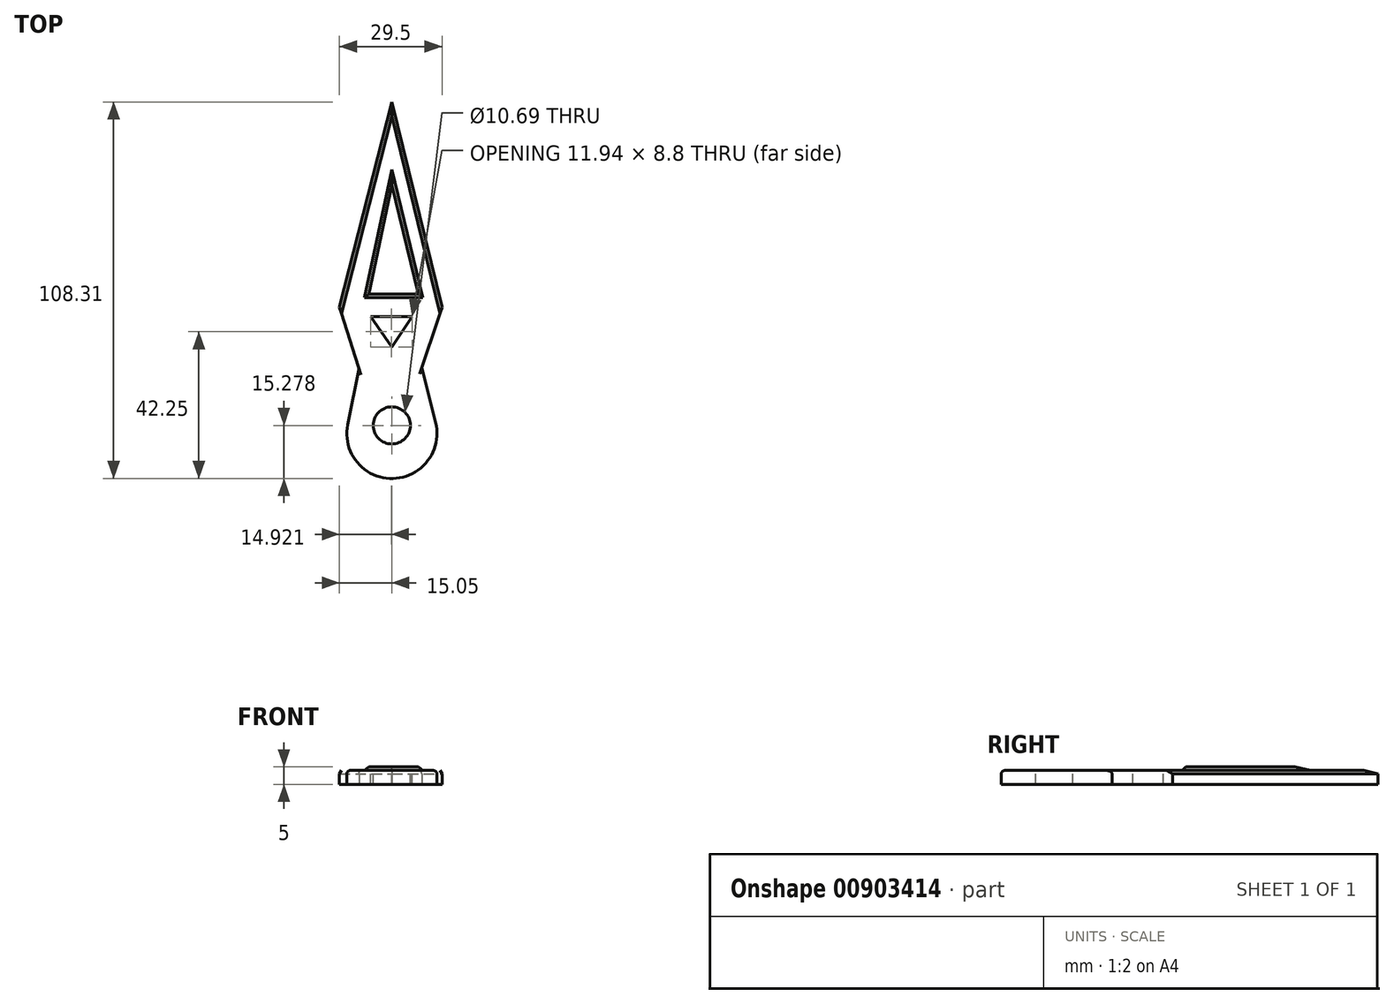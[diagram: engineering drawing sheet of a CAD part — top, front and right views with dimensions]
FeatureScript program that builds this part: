
annotation { "Feature Type Name" : "Feature", "Feature Type Description" : "" }
export const myFeature = defineFeature(function(context is Context, id is Id, definition is map)
    precondition{}
    {
        {
            var Q0;
            Q0=qCreatedBy(makeId("Top.planeOp"),FACE);
            var sketch = newSketch(context, id + "F0", { "sketchPlane" : qUnion([Q0])});
            skLineSegment(sketch, "E0", {"start": v(-15.05, 17.48) * mm, "end": v(14.45, 17.48) * mm});
            skLineSegment(sketch, "E1", {"start": v(-15.05, 17.48) * mm, "end": v(-9.45, 0) * mm});
            skCircle(sketch, "E2", {"center": v(0, -18.9) * mm, "radius": 12.95 * mm});
            skLineSegment(sketch, "E3", {"start": v(14.45, 17.48) * mm, "end": v(8.6, 0) * mm});
            skLineSegment(sketch, "E4", {"start": v(8.6, 0) * mm, "end": v(12.56, -15.73) * mm});
            skLineSegment(sketch, "E5", {"start": v(-9.45, 0) * mm, "end": v(-12.7, -16.36) * mm});
            skLineSegment(sketch, "E6", {"start": v(-15.05, 17.48) * mm, "end": v(0, 76.47) * mm});
            skLineSegment(sketch, "E7", {"start": v(0, 76.47) * mm, "end": v(14.45, 17.48) * mm});
            skSolve(sketch);
        }
        {
            var Q0;
            Q0 = qSketchRegion(id + "F0", true);
            extrude(context, id + "F1", {"entities" : qUnion([Q0]), "depth" : 4 * mm, "offsetDistance" : 25.4 * mm});
        }
        {
            var Q0;
            Q0=makeQuery(id+"F1.opExtrude","CAP_FACE",FACE,{"disambiguationData":[OSD([sQuery(id+"F0.wireOp",EDGE,"E1"),sQuery(id+"F0.wireOp",EDGE,"E2"),sQuery(id+"F0.wireOp",EDGE,"E3"),sQuery(id+"F0.wireOp",EDGE,"E4"),sQuery(id+"F0.wireOp",EDGE,"E5"),sQuery(id+"F0.wireOp",EDGE,"E6"),sQuery(id+"F0.wireOp",EDGE,"E7")])],"isStart":false});
            var sketch = newSketch(context, id + "F2", { "sketchPlane" : qUnion([Q0])});
            skCircle(sketch, "E8", {"center": v(0, -16.56) * mm, "radius": 5.34 * mm});
            skSolve(sketch);
        }
        {
            var Q0;
            Q0 = qSketchRegion(id + "F2", true);
            extrude(context, id + "F3", {"entities" : qUnion([Q0]), "operationType" : NewBodyOperationType.REMOVE, "oppositeDirection" : true, "depth" : 25.4 * mm, "offsetDistance" : 25.4 * mm});
        }
        {
            var Q0;
            Q0=makeQuery(id+"F1.opExtrude","CAP_FACE",FACE,{"disambiguationData":[OSD([sQuery(id+"F0.wireOp",EDGE,"E1"),sQuery(id+"F0.wireOp",EDGE,"E2"),sQuery(id+"F0.wireOp",EDGE,"E3"),sQuery(id+"F0.wireOp",EDGE,"E4"),sQuery(id+"F0.wireOp",EDGE,"E5"),sQuery(id+"F0.wireOp",EDGE,"E6"),sQuery(id+"F0.wireOp",EDGE,"E7")])],"isStart":false});
            var sketch = newSketch(context, id + "F4", { "sketchPlane" : qUnion([Q0])});
            skLineSegment(sketch, "E9", {"start": v(0, 6) * mm, "end": v(-6.1, 14.81) * mm});
            skLineSegment(sketch, "E10", {"start": v(-6.1, 14.81) * mm, "end": v(5.84, 14.81) * mm});
            skLineSegment(sketch, "E11", {"start": v(5.84, 14.81) * mm, "end": v(0, 6) * mm});
            skSolve(sketch);
        }
        {
            var Q0;
            Q0 = qSketchRegion(id + "F4", true);
            extrude(context, id + "F5", {"entities" : qUnion([Q0]), "operationType" : NewBodyOperationType.REMOVE, "oppositeDirection" : true, "depth" : 25.4 * mm, "offsetDistance" : 25.4 * mm});
        }
        {
            var Q0;
            Q0=makeQuery(id+"F1.opExtrude","CAP_FACE",FACE,{"disambiguationData":[OSD([sQuery(id+"F0.wireOp",EDGE,"E1"),sQuery(id+"F0.wireOp",EDGE,"E2"),sQuery(id+"F0.wireOp",EDGE,"E3"),sQuery(id+"F0.wireOp",EDGE,"E4"),sQuery(id+"F0.wireOp",EDGE,"E5"),sQuery(id+"F0.wireOp",EDGE,"E6"),sQuery(id+"F0.wireOp",EDGE,"E7")])],"isStart":false});
            var sketch = newSketch(context, id + "F6", { "sketchPlane" : qUnion([Q0])});
            skLineSegment(sketch, "E12", {"start": v(-7.84, 20.27) * mm, "end": v(8.9, 20.27) * mm});
            skLineSegment(sketch, "E13", {"start": v(8.9, 20.27) * mm, "end": v(0, 57.05) * mm});
            skLineSegment(sketch, "E14", {"start": v(0, 57.05) * mm, "end": v(-7.84, 20.27) * mm});
            skSolve(sketch);
        }
        {
            var Q0;
            Q0 = qSketchRegion(id + "F6", true);
            extrude(context, id + "F7", {"entities" : qUnion([Q0]), "operationType" : NewBodyOperationType.ADD, "depth" : 1 * mm, "offsetDistance" : 25.4 * mm});
        }
        {
            var Q0;
            Q0=makeQuery(id+"F7.opExtrude","CAP_EDGE",EDGE,{"disambiguationData":[OSD([sQuery(id+"F6.wireOp",EDGE,"E14")])],"isStart":false});
            var Q1;
            Q1=makeQuery(id+"F7.opExtrude","CAP_EDGE",EDGE,{"disambiguationData":[OSD([sQuery(id+"F6.wireOp",EDGE,"E13")])],"isStart":false});
            chamfer(context, id + "F8", {"entities" : qUnion([Q0, Q1]), "width" : 1 * mm, "tangentPropagation" : true});
        }
        {
            var Q0;
            Q0=makeQuery(id+"F7.opExtrude","CAP_EDGE",EDGE,{"disambiguationData":[OSD([sQuery(id+"F6.wireOp",EDGE,"E12")])],"isStart":false});
            chamfer(context, id + "F9", {"entities" : qUnion([Q0]), "width" : 1 * mm, "tangentPropagation" : true});
        }
        {
            var Q0;
            Q0=makeQuery(id+"F1.opExtrude","CAP_EDGE",EDGE,{"disambiguationData":[OSD([sQuery(id+"F0.wireOp",EDGE,"E6")])],"isStart":false});
            var Q1;
            Q1=makeQuery(id+"F1.opExtrude","CAP_EDGE",EDGE,{"disambiguationData":[OSD([sQuery(id+"F0.wireOp",EDGE,"E7")])],"isStart":false});
            chamfer(context, id + "F10", {"entities" : qUnion([Q0, Q1]), "width" : 1 * mm, "tangentPropagation" : true});
        }
        {
            var Q0;
            Q0=makeQuery(id+"F1.opExtrude","CAP_EDGE",EDGE,{"disambiguationData":[OSD([sQuery(id+"F0.wireOp",EDGE,"E2")])],"isStart":false});
            fillet(context, id + "F11", {"entities" : qUnion([Q0]), "radius" : 1 * mm, "tangentPropagation" : true, "allowEdgeOverflow" : false});
        }
    });
